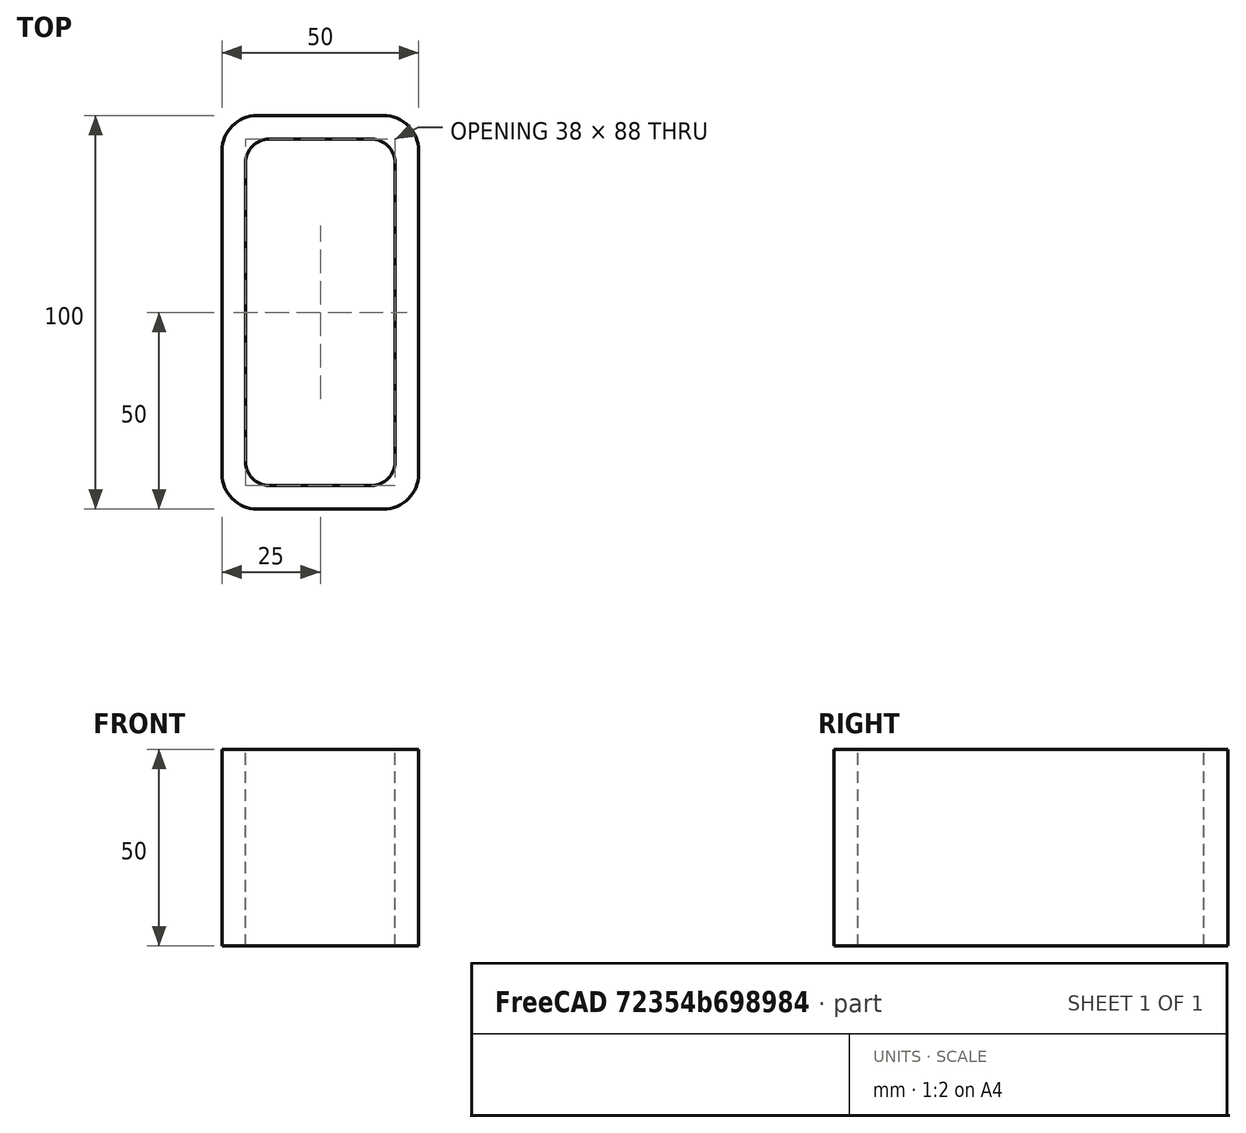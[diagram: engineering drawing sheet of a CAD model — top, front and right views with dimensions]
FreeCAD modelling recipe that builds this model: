
FCSTD DOCUMENT  (FreeCAD 0.15R4671 (Git))
Label: Rectangular hollow section 100x50x6 EN10219 S235JRH
License: All rights reserved
LicenseURL: http://en.wikipedia.org/wiki/All_rights_reserved
objects: Sketcher::SketchObject×1, Part::Extrusion×1
note: 2 computed .brp shape members not serialized (recipe doc carries the construction recipe); baked Part::Feature solids carry a one-line shape summary decoded from their .brp

FEATURE [Sketcher::SketchObject] Sketch
  sketch-geometry (16):
    g0: LineSegment StartX=-13 StartY=44 StartZ=0 EndX=13 EndY=44 EndZ=0
    g1: LineSegment StartX=19 StartY=38 StartZ=0 EndX=19 EndY=-38 EndZ=0
    g2: LineSegment StartX=13 StartY=-44 StartZ=0 EndX=-13 EndY=-44 EndZ=0
    g3: LineSegment StartX=-19 StartY=-38 StartZ=0 EndX=-19 EndY=38 EndZ=0
    g4: LineSegment StartX=-16 StartY=50 StartZ=0 EndX=16 EndY=50 EndZ=0
    g5: LineSegment StartX=25 StartY=41 StartZ=0 EndX=25 EndY=-41 EndZ=0
    g6: LineSegment StartX=16 StartY=-50 StartZ=0 EndX=-16 EndY=-50 EndZ=0
    g7: LineSegment StartX=-25 StartY=-41 StartZ=0 EndX=-25 EndY=41 EndZ=0
    g8: ArcOfCircle CenterX=-13 CenterY=38 CenterZ=0 NormalX=0 NormalY=0 NormalZ=1 Radius=6 StartAngle=1.5708 EndAngle=3.14159
    g9: ArcOfCircle CenterX=13 CenterY=38 CenterZ=0 NormalX=0 NormalY=0 NormalZ=1 Radius=6 StartAngle=0 EndAngle=1.5708
    g10: ArcOfCircle CenterX=13 CenterY=-38 CenterZ=0 NormalX=0 NormalY=0 NormalZ=1 Radius=6 StartAngle=4.71239 EndAngle=6.28319
    g11: ArcOfCircle CenterX=-13 CenterY=-38 CenterZ=0 NormalX=0 NormalY=0 NormalZ=1 Radius=6 StartAngle=3.14159 EndAngle=4.71239
    g12: ArcOfCircle CenterX=16 CenterY=41 CenterZ=0 NormalX=0 NormalY=0 NormalZ=1 Radius=9 StartAngle=0 EndAngle=1.5708
    g13: ArcOfCircle CenterX=16 CenterY=-41 CenterZ=0 NormalX=0 NormalY=0 NormalZ=1 Radius=9 StartAngle=4.71239 EndAngle=6.28319
    g14: ArcOfCircle CenterX=-16 CenterY=-41 CenterZ=0 NormalX=0 NormalY=0 NormalZ=1 Radius=9 StartAngle=3.14159 EndAngle=4.71239
    g15: ArcOfCircle CenterX=-16 CenterY=41 CenterZ=0 NormalX=0 NormalY=0 NormalZ=1 Radius=9 StartAngle=1.5708 EndAngle=3.14159
  constraints (36):
    c: Horizontal(g2)
    c: Vertical(g3)
    c: Horizontal(g6)
    c: Vertical(g7)
    c: Tangent(g3,g8) = 1.5708
    c: Tangent(g0,g8) = 1.5708
    c: Tangent(g0,g9) = 1.5708
    c: Tangent(g1,g9) = 1.5708
    c: Tangent(g1,g10) = 1.5708
    c: Tangent(g2,g10) = 1.5708
    c: Tangent(g2,g11) = 1.5708
    c: Tangent(g3,g11) = 1.5708
    c: Tangent(g4,g12) = 1.5708
    c: Tangent(g5,g12) = 1.5708
    c: Tangent(g5,g13) = 1.5708
    c: Tangent(g6,g13) = 1.5708
    c: Tangent(g6,g14) = 1.5708
    c: Tangent(g7,g14) = 1.5708
    c: Tangent(g7,g15) = 1.5708
    c: Tangent(g4,g15) = 1.5708
    c: Equal(g9,g8)
    c: Equal(g9,g11)
    c: Equal(g9,g10)
    c: Equal(g12,g15)
    c: Equal(g12,g14)
    c: Equal(g12,g13)
    c: Symmetric(g4,g6,g-1)
    c: Symmetric(g7,g5,g-2)
    c: DistanceY(g4,g6) = -100
    c: DistanceX(g7,g5) = 50
    c: Symmetric(g3,g1,g-2)
    c: Symmetric(g0,g2,g-1)
    c: DistanceY(g0,g4) = 6
    c: DistanceX(g5,g1) = -6
    c: Radius(g9) = 6
    c: Radius(g12) = 9
FEATURE [Part::Extrusion] Extrude  label="Rectangular hollow section 100x50x6 EN10219 S235JRH"
  Base = -> Sketch
  Dir = (0,0,50)
  Solid = true
